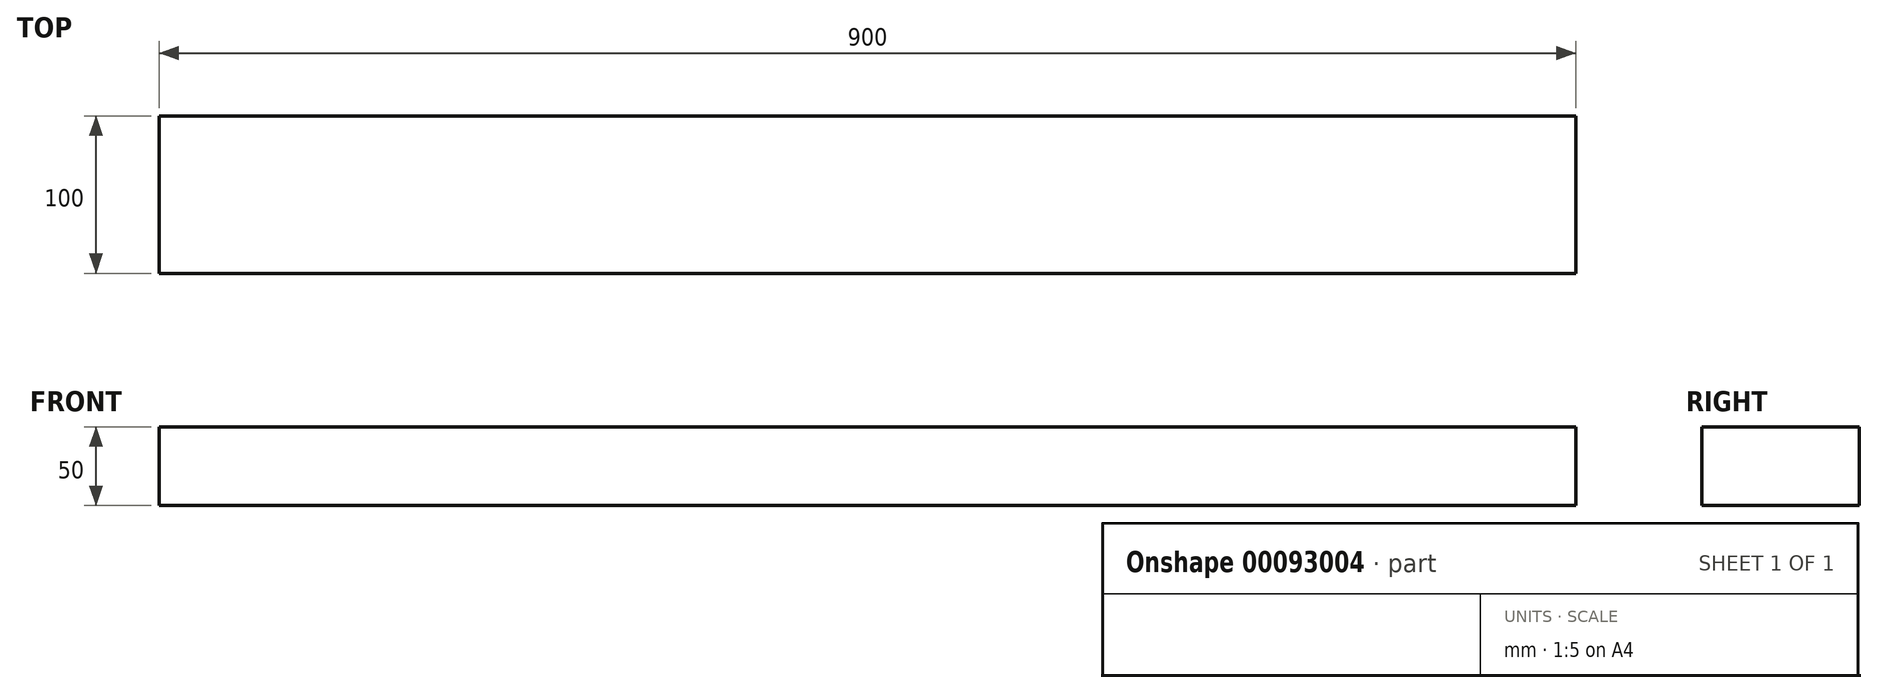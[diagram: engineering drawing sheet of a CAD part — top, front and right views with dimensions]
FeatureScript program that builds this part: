
annotation { "Feature Type Name" : "Feature", "Feature Type Description" : "" }
export const myFeature = defineFeature(function(context is Context, id is Id, definition is map)
    precondition{}
    {
        {
            var Q0;
            Q0=qCreatedBy(makeId("Right.planeOp"),FACE);
            var sketch = newSketch(context, id + "F0", { "sketchPlane" : qUnion([Q0])});
            skLineSegment(sketch, "E0.bottom", {"start": v(-50, 50) * mm, "end": v(50, 50) * mm});
            skLineSegment(sketch, "E0.top", {"start": v(-50, 0) * mm, "end": v(50, 0) * mm});
            skLineSegment(sketch, "E0.left", {"start": v(-50, 50) * mm, "end": v(-50, 0) * mm});
            skLineSegment(sketch, "E0.right", {"start": v(50, 50) * mm, "end": v(50, 0) * mm});
            skSolve(sketch);
        }
        {
            var Q0;
            Q0=makeQuery(id+"F0.imprint","IMPRINT",FACE,{"disambiguationData":[TD([[makeQuery(id+"F0.imprint","IMPRINT",EDGE,{"derivedFrom":sQuery(id+"F0.wireOp",EDGE,"E0.bottom")}),-1.0]])]});
            extrude(context, id + "F1", {"entities" : qUnion([Q0]), "endBound" : BoundingType.SYMMETRIC, "depth" : 900 * mm});
        }
    });
